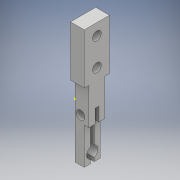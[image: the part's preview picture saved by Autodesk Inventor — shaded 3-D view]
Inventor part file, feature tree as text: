
AUTODESK INVENTOR PART (.ipt)
format: ipt  version: 2017 (Build 210142000, 142)  size: 163,328 bytes
history: native  units: mm
features: sketch x5, extrude x4
ambient origin geometry x8: Origin, YZ Plane, XZ Plane, XY Plane, X Axis, Y Axis, Z Axis, Center Point
bodies: Solid1 (feature_tree)
feature tree (9):
  extrude  "Extrusion1"  Depth=2.0mm
  extrude  "Extrusion2"  Depth=8.0mm
  sketch  "Sketch4"  dims[d11=3.0mm d12=1.8mm]
  extrude  "Extrusion3"  Depth=3.0mm
  extrude  "Extrusion4"  Depth=2.0mm
  sketch  "Sketch2"  dims[d1=10.0mm d2=2.0mm]
  sketch  "Sketch3"  dims[d9=1.9mm d10=8.0mm]
  sketch  "Sketch5"  dims[d13=3.5mm d14=0.0mm d15=2.5mm d16=2.0mm]
  sketch  "Sketch6"  dims[d17=0.4mm d18=11.0mm d19=0.8mm d20=10.0mm d21=0.0mm d23=1.0mm d24=1.0mm d25=3.0mm d26=0.0mm d27=5.0mm d28=2.75mm d32=1.9mm d33=2.5mm d34=1.9mm d35=6.0mm d36=3.0mm d37=0.0mm d38=4.0mm d39=5.5mm d40=4.0mm]
